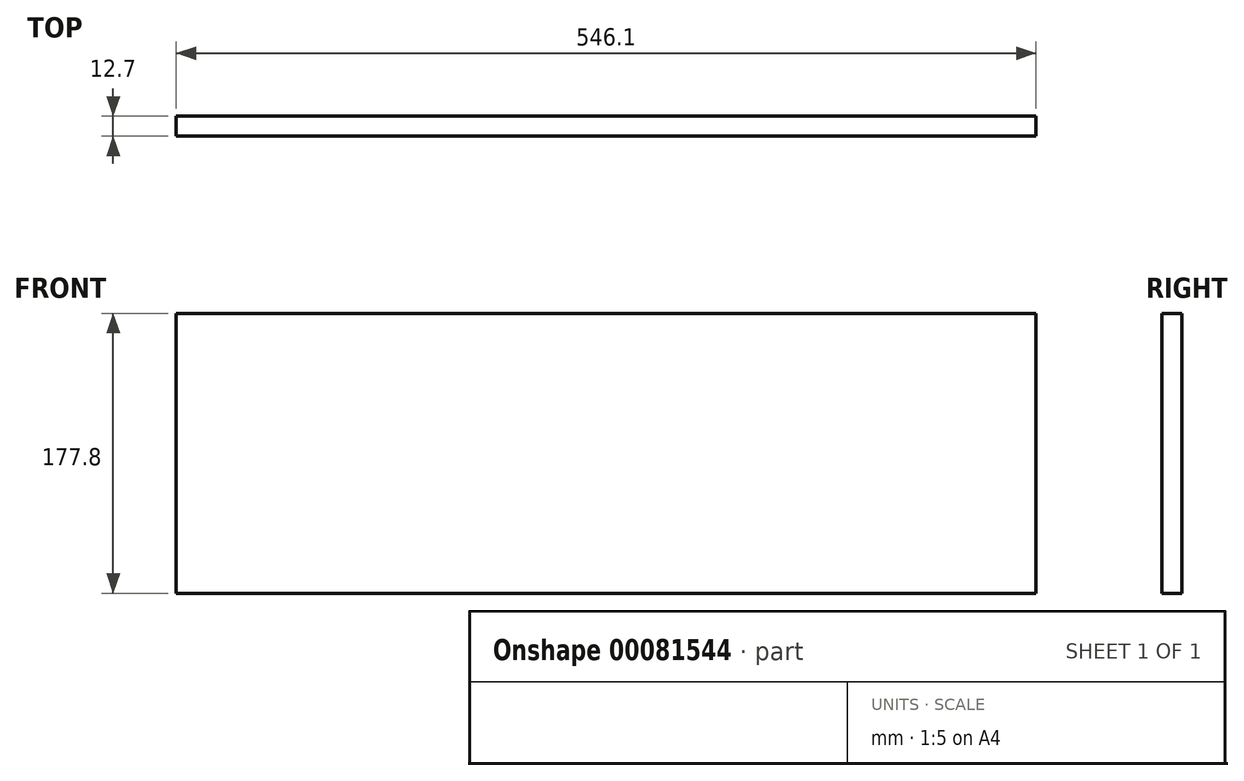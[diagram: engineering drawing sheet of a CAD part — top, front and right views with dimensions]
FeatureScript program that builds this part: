
annotation { "Feature Type Name" : "Feature", "Feature Type Description" : "" }
export const myFeature = defineFeature(function(context is Context, id is Id, definition is map)
    precondition{}
    {
        {
            var Q0;
            Q0=qCreatedBy(makeId("Front.planeOp"),FACE);
            var sketch = newSketch(context, id + "F0", { "sketchPlane" : qUnion([Q0])});
            skLineSegment(sketch, "E0.bottom", {"start": v(-273.05, 88.9) * mm, "end": v(273.05, 88.9) * mm});
            skLineSegment(sketch, "E0.top", {"start": v(-273.05, -88.9) * mm, "end": v(273.05, -88.9) * mm});
            skLineSegment(sketch, "E0.left", {"start": v(-273.05, 88.9) * mm, "end": v(-273.05, -88.9) * mm});
            skLineSegment(sketch, "E0.right", {"start": v(273.05, 88.9) * mm, "end": v(273.05, -88.9) * mm});
            skPoint(sketch, "E0.middle", {"position": v(0, 0) * mm});
            skSolve(sketch);
        }
        {
            var Q0;
            Q0=makeQuery(id+"F0.imprint","IMPRINT",FACE,{"disambiguationData":[TD([[makeQuery(id+"F0.imprint","IMPRINT",EDGE,{"derivedFrom":sQuery(id+"F0.wireOp",EDGE,"E0.bottom")}),-1.0]])]});
            extrude(context, id + "F1", {"entities" : qUnion([Q0]), "depth" : 12.7 * mm});
        }
    });
